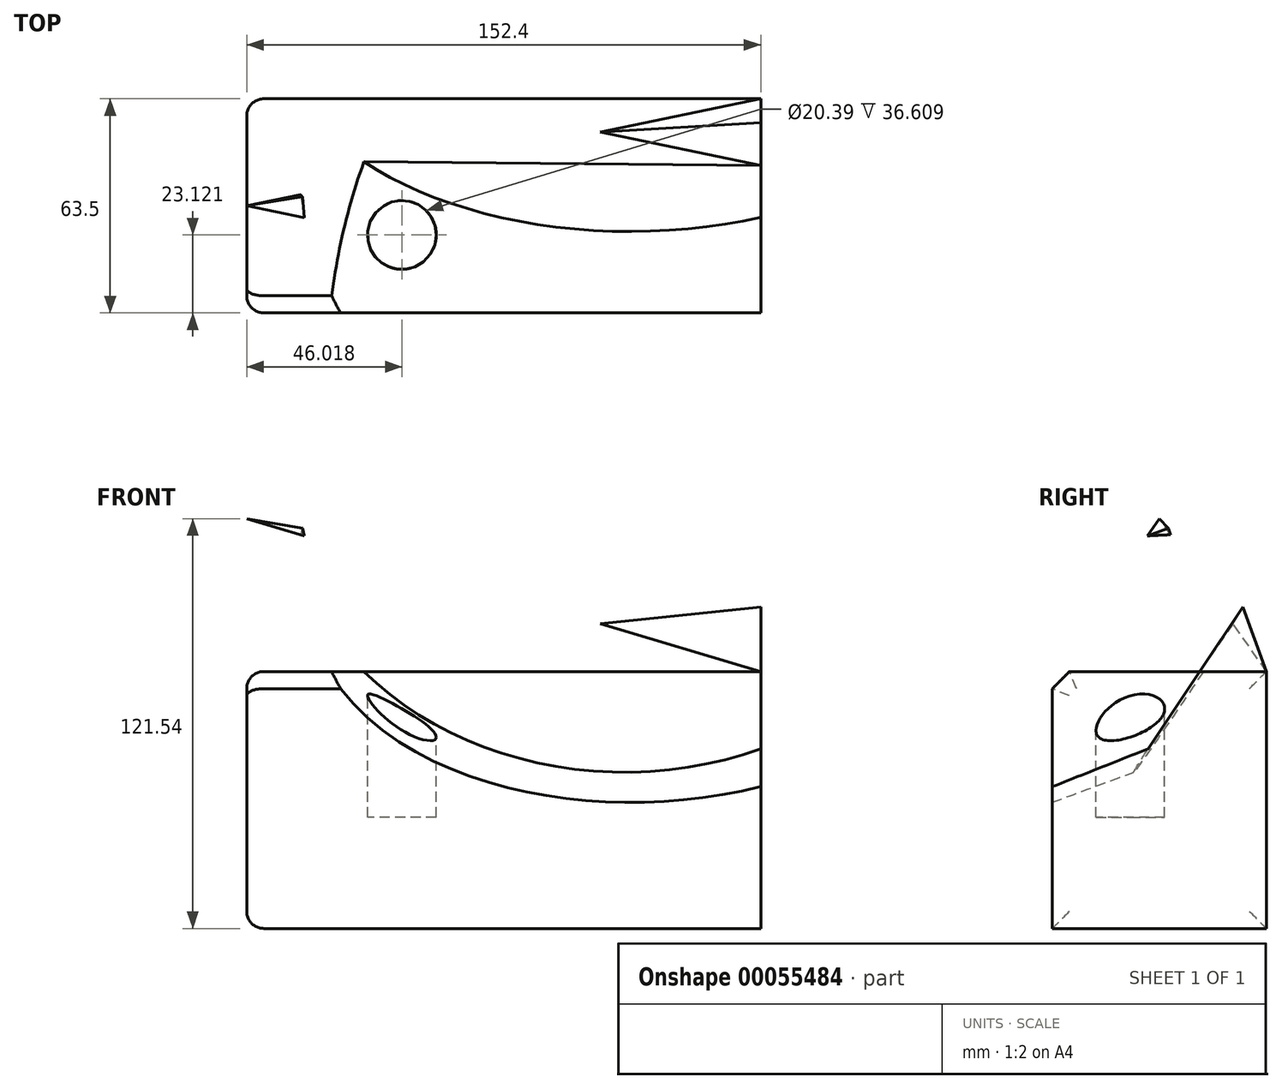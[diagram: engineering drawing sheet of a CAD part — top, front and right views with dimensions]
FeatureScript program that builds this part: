
annotation { "Feature Type Name" : "Feature", "Feature Type Description" : "" }
export const myFeature = defineFeature(function(context is Context, id is Id, definition is map)
    precondition{}
    {
        {
            var Q0;
            Q0=qCreatedBy(makeId("Top.planeOp"),FACE);
            var sketch = newSketch(context, id + "F0", { "sketchPlane" : qUnion([Q0])});
            skLineSegment(sketch, "E0.bottom", {"start": v(0, 0) * mm, "end": v(152.4, 0) * mm});
            skLineSegment(sketch, "E0.top", {"start": v(0, 63.5) * mm, "end": v(152.4, 63.5) * mm});
            skLineSegment(sketch, "E0.left", {"start": v(0, 0) * mm, "end": v(0, 63.5) * mm});
            skLineSegment(sketch, "E0.right", {"start": v(152.4, 0) * mm, "end": v(152.4, 63.5) * mm});
            skSolve(sketch);
        }
        {
            var Q0;
            Q0=makeQuery(id+"F0.imprint","IMPRINT",FACE,{"disambiguationData":[TD([[makeQuery(id+"F0.imprint","IMPRINT",EDGE,{"derivedFrom":sQuery(id+"F0.wireOp",EDGE,"E0.bottom")}),1.0]])]});
            extrude(context, id + "F1", {"entities" : qUnion([Q0]), "depth" : 76.2 * mm});
        }
        {
            var Q0;
            Q0=makeQuery(id+"F1.opExtrude","SWEPT_FACE",FACE,{"disambiguationData":[OSD([sQuery(id+"F0.wireOp",EDGE,"E0.right")])]});
            var sketch = newSketch(context, id + "F2", { "sketchPlane" : qUnion([Q0])});
            skLineSegment(sketch, "E1", {"start": v(0, 76.2) * mm, "end": v(40.86, 137.43) * mm});
            skLineSegment(sketch, "E2", {"start": v(40.86, 137.43) * mm, "end": v(63.5, 76.2) * mm});
            skLineSegment(sketch, "E3", {"start": v(63.5, 76.2) * mm, "end": v(0, 76.2) * mm});
            skSolve(sketch);
        }
        {
            var Q0;
            Q0=makeQuery(id+"F1.opExtrude","SWEPT_FACE",FACE,{"disambiguationData":[OSD([sQuery(id+"F0.wireOp",EDGE,"E0.left")])]});
            var sketch = newSketch(context, id + "F3", { "sketchPlane" : qUnion([Q0])});
            skPoint(sketch, "E4", {"position": v(-31.75, 121.54) * mm});
            skPoint(sketch, "E4.positionSnap0", {"position": v(-31.75, 76.2) * mm});
            skSolve(sketch);
        }
        {
            var Q0;
            Q0=makeQuery(id+"F1.opExtrude","CAP_FACE",FACE,{"disambiguationData":[OSD([sQuery(id+"F0.wireOp",EDGE,"E0.bottom"),sQuery(id+"F0.wireOp",EDGE,"E0.top"),sQuery(id+"F0.wireOp",EDGE,"E0.left"),sQuery(id+"F0.wireOp",EDGE,"E0.right")])],"isStart":false});
            var sketch = newSketch(context, id + "F4", { "sketchPlane" : qUnion([Q0])});
            skCircle(sketch, "E5", {"center": v(46.02, 23.12) * mm, "radius": 10.2 * mm});
            skSolve(sketch);
        }
        {
            var Q0;
            Q0=makeQuery(id+"F4.imprint","IMPRINT",FACE,{"disambiguationData":[TD([[makeQuery(id+"F4.imprint","IMPRINT",EDGE,{"derivedFrom":sQuery(id+"F4.wireOp",EDGE,"E5")}),1.0]])]});
            extrude(context, id + "F5", {"entities" : qUnion([Q0]), "operationType" : NewBodyOperationType.REMOVE, "oppositeDirection" : true, "depth" : 43.23 * mm});
        }
        {
            var Q0;
            Q0=makeQuery(id+"F2.imprint","IMPRINT",FACE,{"disambiguationData":[TD([[makeQuery(id+"F2.imprint","IMPRINT",EDGE,{"derivedFrom":sQuery(id+"F2.wireOp",EDGE,"E1")}),-1.0]])]});
            var Q1;
            Q1=sQuery(id+"F3.wireOp",VERTEX,"E4");
            loft(context, id + "F6", {"sheetProfilesArray" : [{ "sheetProfileEntities" : qUnion([Q0]) }, { "sheetProfileEntities" : qUnion([Q1]) }]});
        }
        {
            var Q0;
            Q0=makeQuery(id+"F1.opExtrude","CAP_EDGE",EDGE,{"disambiguationData":[OSD([sQuery(id+"F0.wireOp",EDGE,"E0.bottom")])],"isStart":false});
            chamfer(context, id + "F7", {"entities" : qUnion([Q0]), "width" : 5.08 * mm, "tangentPropagation" : true});
        }
        {
            var Q0;
            Q0=makeQuery(id+"F1.opExtrude","SWEPT_FACE",FACE,{"disambiguationData":[OSD([sQuery(id+"F0.wireOp",EDGE,"E0.left")])]});
            fillet(context, id + "F8", {"entities" : qUnion([Q0]), "radius" : 5.08 * mm, "tangentPropagation" : true, "allowEdgeOverflow" : false});
        }
        {
            var Q0;
            Q0=makeQuery(id+"F6.opLoft","SWEPT_FACE",FACE,{"disambiguationData":[OSD([sQuery(id+"F0.wireOp",EDGE,"E0.bottom"),sQuery(id+"F0.wireOp",EDGE,"E0.right"),sQuery(id+"F2.wireOp",EDGE,"E1"),sQuery(id+"F2.wireOp",EDGE,"E2"),sQuery(id+"F2.wireOp",EDGE,"E3")])]});
            var sketch = newSketch(context, id + "F9", { "sketchPlane" : qUnion([Q0])});
            skCircle(sketch, "E6", {"center": v(118.67, 103.48) * mm, "radius": 101.6 * mm});
            skSolve(sketch);
        }
        {
            var Q0;
            Q0=makeQuery(id+"F6.opLoft","SWEPT_FACE",FACE,{"disambiguationData":[OSD([sQuery(id+"F0.wireOp",EDGE,"E0.top"),sQuery(id+"F0.wireOp",EDGE,"E0.right"),sQuery(id+"F2.wireOp",EDGE,"E1"),sQuery(id+"F2.wireOp",EDGE,"E2"),sQuery(id+"F2.wireOp",EDGE,"E3")])]});
            var Q1;
            {var subQ2=sQuery(id+"F2.wireOp",EDGE,"E3");var subQ3=sQuery(id+"F2.wireOp",EDGE,"E1");var subQ4=sQuery(id+"F0.wireOp",EDGE,"E0.right");var subQ5=sQuery(id+"F0.wireOp",EDGE,"E0.bottom");var subQ8=sQuery(id+"F2.wireOp",EDGE,"E2");var subQ11=makeQuery(id+"F6.opLoft","MID_CAP_EDGE",EDGE,{"disambiguationData":[OSD([subQ5,subQ4,subQ3,subQ8,subQ2])],"capPos":0.0});Q1=makeQuery(id+"F9.imprint","IMPRINT",FACE,{"disambiguationData":[TD([[makeQuery(id+"F9.imprint","IMPRINT",EDGE,{"derivedFrom":subQ11}),1.0]])]});}
            var Q2;
            {var subQ2=sQuery(id+"F2.wireOp",EDGE,"E3");var subQ3=sQuery(id+"F2.wireOp",EDGE,"E1");var subQ4=sQuery(id+"F0.wireOp",EDGE,"E0.right");var subQ5=sQuery(id+"F0.wireOp",EDGE,"E0.bottom");var subQ8=sQuery(id+"F2.wireOp",EDGE,"E2");var subQ11=makeQuery(id+"F6.opLoft","MID_CAP_EDGE",EDGE,{"disambiguationData":[OSD([subQ5,subQ4,subQ3,subQ8,subQ2])],"capPos":0.0});Q2=makeQuery(id+"F9.imprint","IMPRINT",FACE,{"disambiguationData":[TD([[makeQuery(id+"F9.imprint","IMPRINT",EDGE,{"derivedFrom":subQ11}),-1.0]])]});}
            var Q3;
            Q3=makeQuery(id+"F6.opLoft","SWEPT_FACE",FACE,{"disambiguationData":[OSD([sQuery(id+"F0.wireOp",EDGE,"E0.bottom"),sQuery(id+"F0.wireOp",EDGE,"E0.right"),sQuery(id+"F2.wireOp",EDGE,"E1"),sQuery(id+"F2.wireOp",EDGE,"E2"),sQuery(id+"F2.wireOp",EDGE,"E3")])]});
            extrude(context, id + "F10", {"entities" : qUnion([Q0, Q1, Q2, Q3]), "operationType" : NewBodyOperationType.REMOVE, "depth" : 62.15 * mm});
        }
    });
